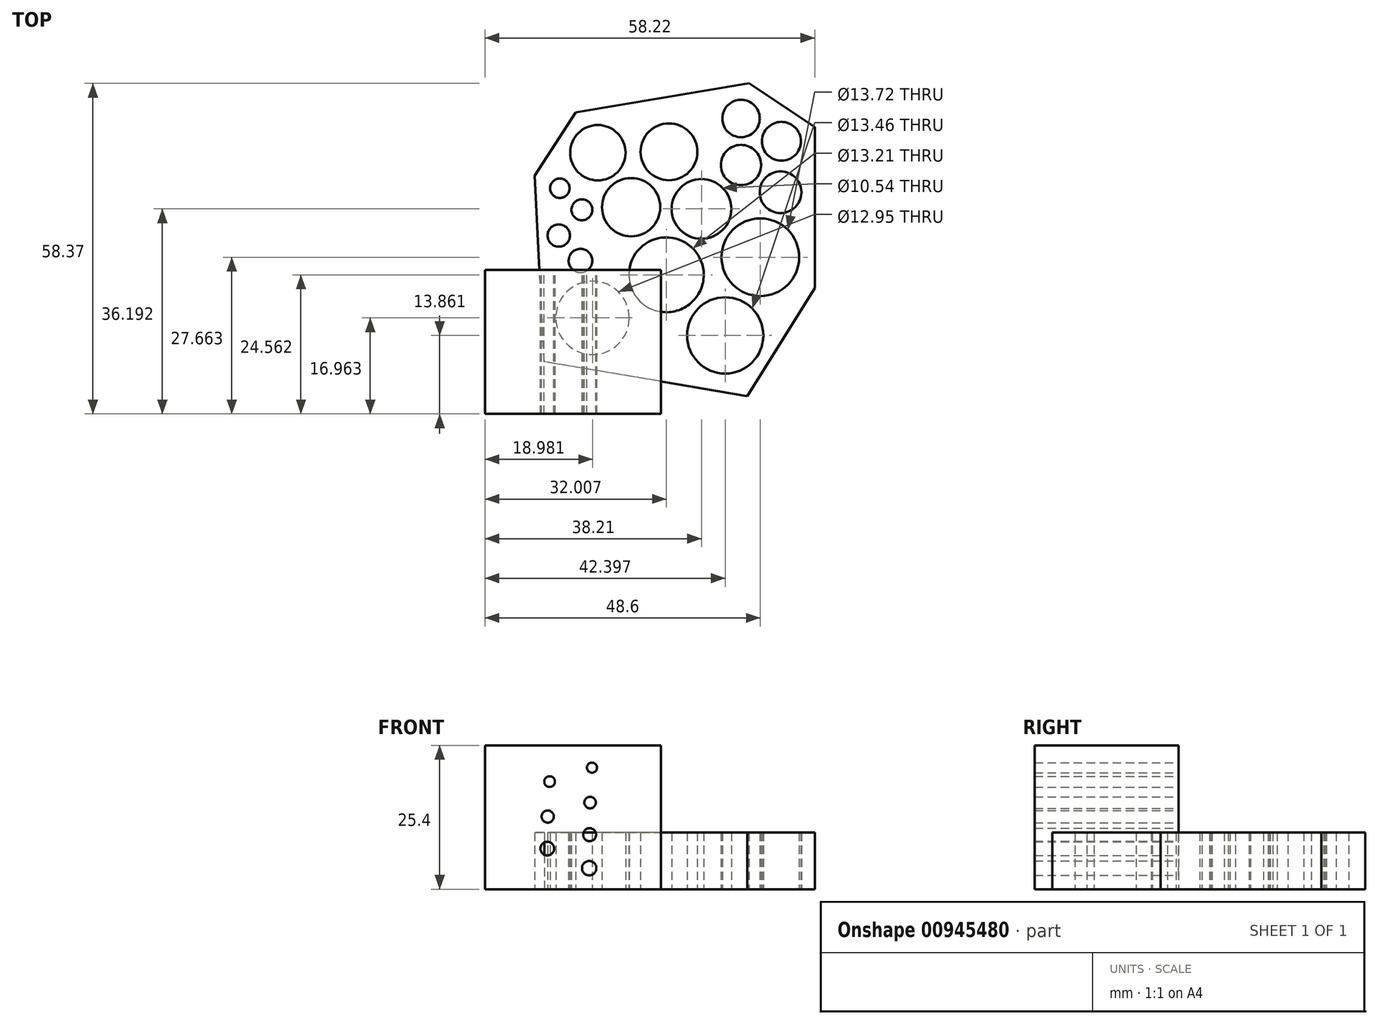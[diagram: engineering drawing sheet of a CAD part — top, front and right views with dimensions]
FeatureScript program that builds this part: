
annotation { "Feature Type Name" : "Feature", "Feature Type Description" : "" }
export const myFeature = defineFeature(function(context is Context, id is Id, definition is map)
    precondition{}
    {
        {
            var Q0;
            Q0=qCreatedBy(makeId("Top.planeOp"),FACE);
            var sketch = newSketch(context, id + "F0", { "sketchPlane" : qUnion([Q0])});
            skCircle(sketch, "E0", {"center": v(-8.7, 10.64) * mm, "radius": 1.84 * mm});
            skCircle(sketch, "E1", {"center": v(-12.77, 6.1) * mm, "radius": 1.97 * mm});
            skCircle(sketch, "E2", {"center": v(-8.94, 1.65) * mm, "radius": 2.1 * mm});
            skCircle(sketch, "E3", {"center": v(-12.59, 14.44) * mm, "radius": 1.71 * mm});
            skCircle(sketch, "E4", {"center": v(-5.88, 20.72) * mm, "radius": 4.89 * mm});
            skCircle(sketch, "E5", {"center": v(6.68, 20.87) * mm, "radius": 5.02 * mm});
            skCircle(sketch, "E6", {"center": v(0, 11.1) * mm, "radius": 5.14 * mm});
            skCircle(sketch, "E7", {"center": v(12.42, 10.8) * mm, "radius": 5.27 * mm});
            skCircle(sketch, "E8", {"center": v(19.4, 26.77) * mm, "radius": 3.3 * mm});
            skCircle(sketch, "E9", {"center": v(26.53, 22.73) * mm, "radius": 3.43 * mm});
            skCircle(sketch, "E10", {"center": v(19.4, 18.55) * mm, "radius": 3.56 * mm});
            skCircle(sketch, "E11", {"center": v(26.38, 13.74) * mm, "radius": 3.68 * mm});
            skCircle(sketch, "E12", {"center": v(6.22, -0.84) * mm, "radius": 6.6 * mm});
            skCircle(sketch, "E13", {"center": v(16.6, -11.54) * mm, "radius": 6.73 * mm});
            skCircle(sketch, "E14", {"center": v(22.81, 2.26) * mm, "radius": 6.86 * mm});
            skCircle(sketch, "E15", {"center": v(-6.8, -8.44) * mm, "radius": 6.48 * mm});
            skLineSegment(sketch, "E16", {"start": v(-17.04, 16.69) * mm, "end": v(-9.76, 27.85) * mm});
            skLineSegment(sketch, "E17", {"start": v(-9.76, 27.85) * mm, "end": v(20.8, 32.97) * mm});
            skLineSegment(sketch, "E18", {"start": v(20.8, 32.97) * mm, "end": v(32.43, 25.21) * mm});
            skLineSegment(sketch, "E19", {"start": v(32.43, 25.21) * mm, "end": v(32.43, -3.16) * mm});
            skLineSegment(sketch, "E20", {"start": v(32.43, -3.16) * mm, "end": v(20.48, -22.24) * mm});
            skLineSegment(sketch, "E21", {"start": v(20.48, -22.24) * mm, "end": v(-15.34, -16.2) * mm});
            skLineSegment(sketch, "E22", {"start": v(-15.34, -16.2) * mm, "end": v(-17.04, 16.69) * mm});
            skSolve(sketch);
        }
        {
            var Q0;
            Q0=qSketchRegion(id+"F0",true);
            extrude(context, id + "F1", {"entities" : qUnion([Q0]), "depth" : 10 * mm});
        }
        {
            var Q0;
            Q0=qCreatedBy(makeId("Front.planeOp"),FACE);
            var sketch = newSketch(context, id + "F2", { "sketchPlane" : qUnion([Q0])});
            skLineSegment(sketch, "E23.bottom", {"start": v(-25.8, 25.4) * mm, "end": v(5.28, 25.4) * mm});
            skLineSegment(sketch, "E23.top", {"start": v(-25.8, 0) * mm, "end": v(5.28, 0) * mm});
            skLineSegment(sketch, "E23.left", {"start": v(-25.8, 25.4) * mm, "end": v(-25.8, 0) * mm});
            skLineSegment(sketch, "E23.right", {"start": v(5.28, 25.4) * mm, "end": v(5.28, 0) * mm});
            skCircle(sketch, "E24", {"center": v(-7.4, 3.7) * mm, "radius": 1.27 * mm});
            skCircle(sketch, "E25", {"center": v(-7.32, 9.62) * mm, "radius": 1.14 * mm});
            skCircle(sketch, "E26", {"center": v(-7.24, 15.3) * mm, "radius": 1.02 * mm});
            skCircle(sketch, "E27", {"center": v(-6.91, 21.45) * mm, "radius": 0.89 * mm});
            skCircle(sketch, "E28", {"center": v(-14.8, 7.16) * mm, "radius": 1.2 * mm});
            skCircle(sketch, "E29", {"center": v(-14.72, 12.83) * mm, "radius": 1.08 * mm});
            skCircle(sketch, "E30", {"center": v(-14.39, 18.99) * mm, "radius": 0.95 * mm});
            skSolve(sketch);
        }
        {
            var Q0;
            Q0=qSketchRegion(id+"F2",true);
            extrude(context, id + "F3", {"entities" : qUnion([Q0]), "depth" : 25.4 * mm});
        }
    });
